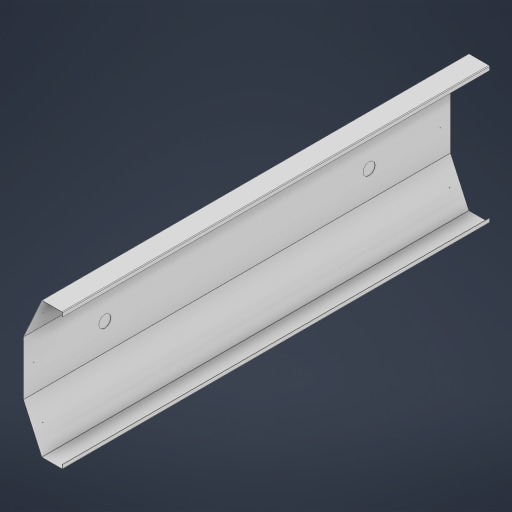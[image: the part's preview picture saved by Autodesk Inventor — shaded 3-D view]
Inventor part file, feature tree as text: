
AUTODESK INVENTOR PART (.ipt)
format: ipt  version: 2024 (Build 280153000, 153)  size: 288,768 bytes
history: native  units: mm
features: other x5, sketch x5, extrude x4
ambient origin geometry x8: Origin, YZ Plane, XZ Plane, XY Plane, X Axis, Y Axis, Z Axis, Center Point
bodies: Body1 (feature_tree)
feature tree (14):
  other  "Sólido1"
  other  "Pestaña de contorno1"
  extrude  "Extrusión1"  Depth=0.5mm
  extrude  "Extrusión2"  Depth=1.0mm
  extrude  "Extrusión3"  Depth=629.96mm
  extrude  "Extrusión4"  Depth=0.5mm
  sketch  "Boceto1"  dims[d5=0.5mm d6=0.5mm]
  other  "Placa1"
  other  "Doblez1"
  other  "Esquina1"
  sketch  "Boceto2"  dims[d7=0.25mm d8=1.0mm]
  sketch  "Boceto3"  dims[d9=0.5mm d10=629.96mm]
  sketch  "Boceto4"  dims[d11=0.5mm d12=0.5mm]
  sketch  "Boceto6"  dims[d13=2.0mm d14=0.5mm d15=0.5mm d16=1.0mm d17=15.0mm d18=1.0mm d19=15.0mm d20=10.0mm d21=0.0mm d22=60.0mm d23=60.0mm d24=30.0mm d25=30.0mm d26=200.0mm d27=0.0mm d28=1.0mm d29=15.0mm d30=1.0mm d31=15.0mm d32=4.25mm d33=0.0mm d34=1.0mm d35=15.0mm d36=1.0mm d37=15.0mm d38=6.0mm d39=0.0mm d40=18.0mm d41=18.0mm d42=120.0mm d43=120.0mm d44=57.156488mm d45=1.0mm d46=0.0mm]
